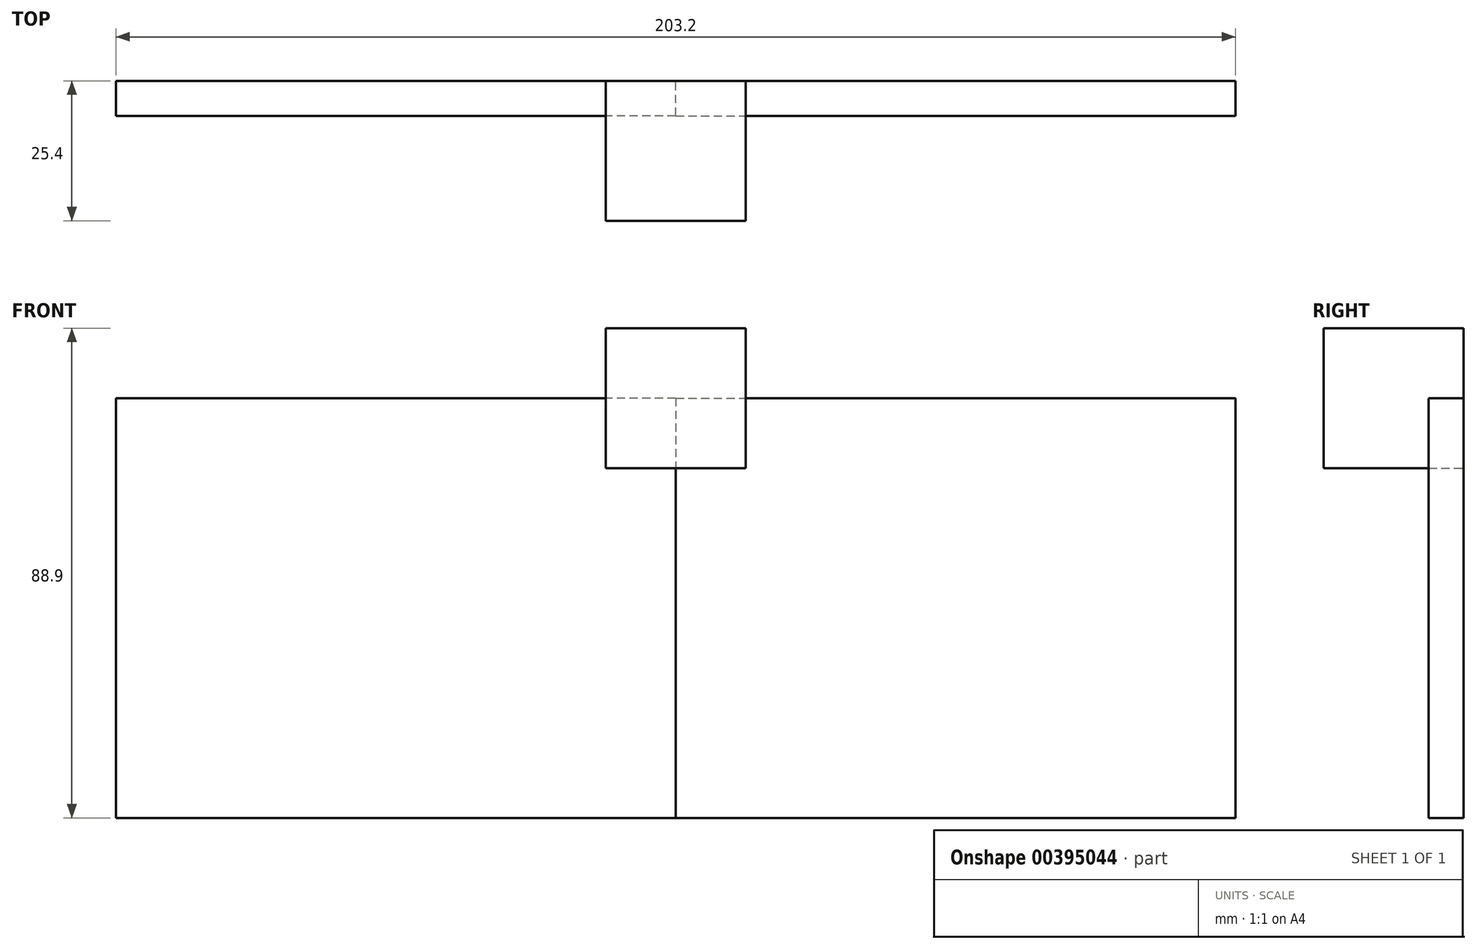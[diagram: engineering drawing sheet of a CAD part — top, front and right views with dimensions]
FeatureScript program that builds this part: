
annotation { "Feature Type Name" : "Feature", "Feature Type Description" : "" }
export const myFeature = defineFeature(function(context is Context, id is Id, definition is map)
    precondition{}
    {
        {
            var Q0;
            Q0=qCreatedBy(makeId("Front.planeOp"),FACE);
            var sketch = newSketch(context, id + "F0", { "sketchPlane" : qUnion([Q0])});
            skLineSegment(sketch, "E0.bottom", {"start": v(12.7, -12.7) * mm, "end": v(-12.7, -12.7) * mm});
            skLineSegment(sketch, "E0.top", {"start": v(12.7, 12.7) * mm, "end": v(-12.7, 12.7) * mm});
            skLineSegment(sketch, "E0.left", {"start": v(12.7, -12.7) * mm, "end": v(12.7, 12.7) * mm});
            skLineSegment(sketch, "E0.right", {"start": v(-12.7, -12.7) * mm, "end": v(-12.7, 12.7) * mm});
            skPoint(sketch, "E0.middle", {"position": v(0, 0) * mm});
            skSolve(sketch);
        }
        {
            var Q0;
            Q0=qCreatedBy(makeId("Front.planeOp"),FACE);
            var sketch = newSketch(context, id + "F1", { "sketchPlane" : qUnion([Q0])});
            skLineSegment(sketch, "E1.bottom", {"start": v(0, 0) * mm, "end": v(101.6, 0) * mm});
            skLineSegment(sketch, "E1.top", {"start": v(0, -76.2) * mm, "end": v(101.6, -76.2) * mm});
            skLineSegment(sketch, "E1.left", {"start": v(0, 0) * mm, "end": v(0, -76.2) * mm});
            skLineSegment(sketch, "E1.right", {"start": v(101.6, 0) * mm, "end": v(101.6, -76.2) * mm});
            skSolve(sketch);
        }
        {
            var Q0;
            Q0=qCreatedBy(makeId("Front.planeOp"),FACE);
            var sketch = newSketch(context, id + "F2", { "sketchPlane" : qUnion([Q0])});
            skLineSegment(sketch, "E2.bottom", {"start": v(0, 0) * mm, "end": v(-101.6, 0) * mm});
            skLineSegment(sketch, "E2.top", {"start": v(0, -76.2) * mm, "end": v(-101.6, -76.2) * mm});
            skLineSegment(sketch, "E2.left", {"start": v(0, 0) * mm, "end": v(0, -76.2) * mm});
            skLineSegment(sketch, "E2.right", {"start": v(-101.6, 0) * mm, "end": v(-101.6, -76.2) * mm});
            skSolve(sketch);
        }
        {
            var Q0;
            Q0=makeQuery(id+"F2.imprint","IMPRINT",FACE,{"disambiguationData":[TD([[makeQuery(id+"F2.imprint","IMPRINT",EDGE,{"derivedFrom":sQuery(id+"F2.wireOp",EDGE,"E2.bottom")}),1.0]])]});
            var Q1;
            Q1=makeQuery(id+"F1.imprint","IMPRINT",FACE,{"disambiguationData":[TD([[makeQuery(id+"F1.imprint","IMPRINT",EDGE,{"derivedFrom":sQuery(id+"F1.wireOp",EDGE,"E1.bottom")}),-1.0]])]});
            extrude(context, id + "F3", {"entities" : qUnion([Q0, Q1]), "depth" : 6.35 * mm});
        }
        {
            var Q0;
            Q0=makeQuery(id+"F0.imprint","IMPRINT",FACE,{"disambiguationData":[TD([[makeQuery(id+"F0.imprint","IMPRINT",EDGE,{"derivedFrom":sQuery(id+"F0.wireOp",EDGE,"E0.bottom")}),-1.0]])]});
            extrude(context, id + "F4", {"entities" : qUnion([Q0]), "depth" : 25.4 * mm});
        }
    });
